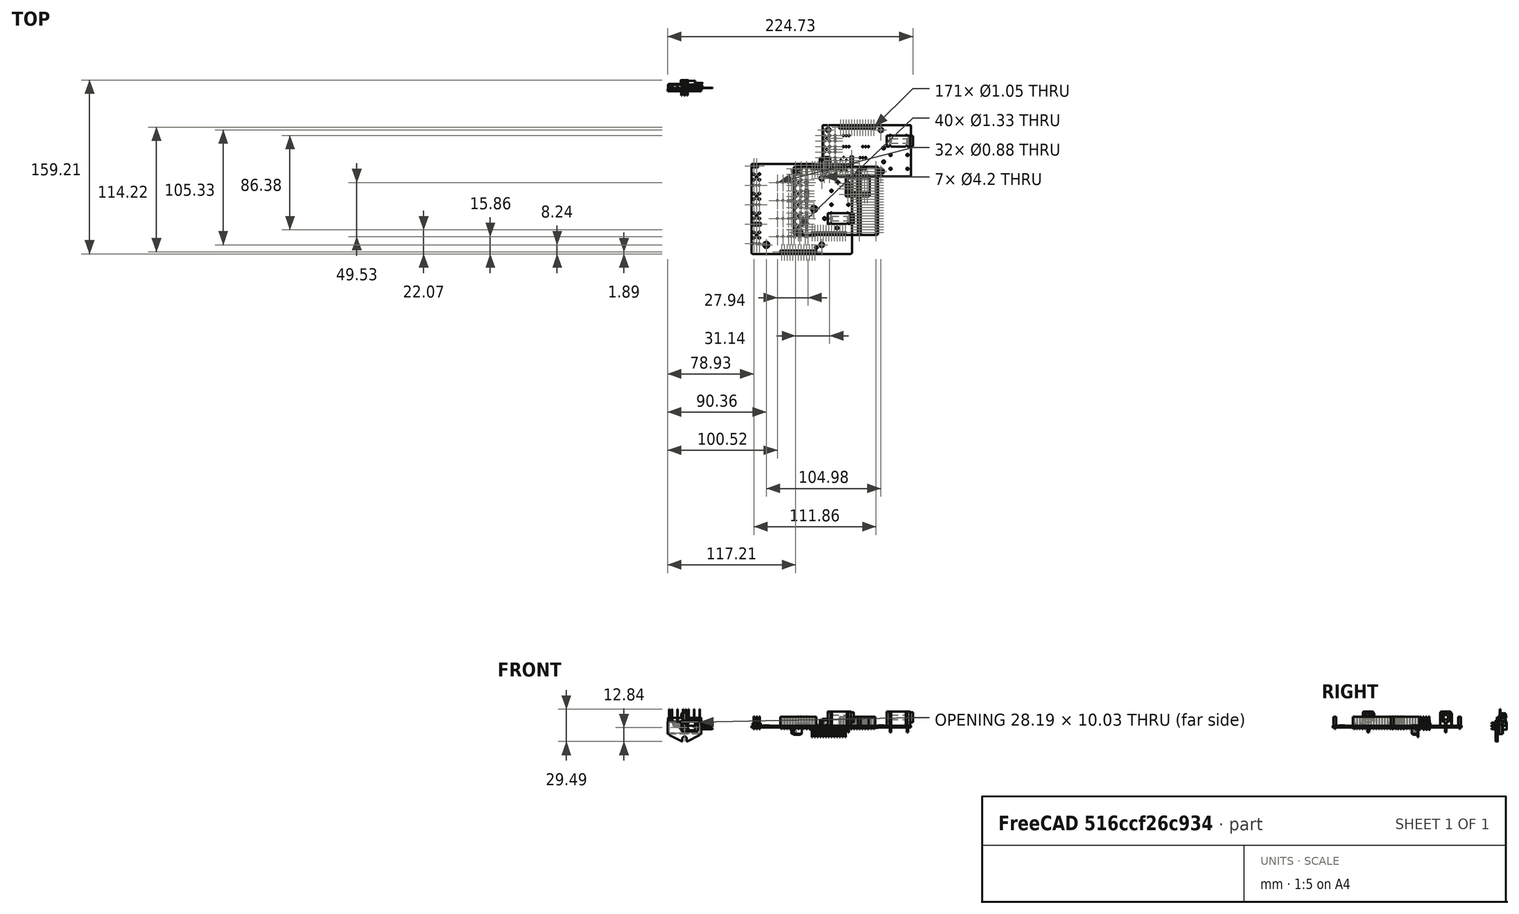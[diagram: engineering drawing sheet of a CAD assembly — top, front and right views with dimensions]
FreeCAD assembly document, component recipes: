
FREECAD ASSEMBLY — COMPONENT RECIPES ("KiCadStepUp")

This assembly document has 4 components, labeled P0..P3 below (a component is one placed body or linked part). 0 of them carry a construction recipe — the FreeCAD feature program that regenerates the part from scratch, quoted from this document or its linked companion documents; the rest are supplied as boundary geometry only. No exploded tour is included for this assembly.
COMPONENT P0 — geometry summary ("TIA1"; no construction recipe available for this part):
  bounding box: 21.8 x 19.0 x 11.6 mm
  tessellated surface: 5,376 triangles
  volume: 1532 mm^3 (32% of its bounding box)
  symmetry: mirror-symmetric across its x mid-plane
COMPONENT P1 — geometry summary ("HighVoltageBoard"; no construction recipe available for this part):
  bounding box: 100.7 x 82.5 x 29.5 mm
  tessellated surface: 122,468 triangles
  volume: 30977 mm^3 (13% of its bounding box)
COMPONENT P2 — geometry summary ("MainBoard"; no construction recipe available for this part):
  bounding box: 79.5 x 62.5 x 18.9 mm
  tessellated surface: 98,262 triangles
  volume: 13681 mm^3 (15% of its bounding box)
COMPONENT P3 — geometry summary ("PowerBoard"; no construction recipe available for this part):
  bounding box: 85.4 x 47.1 x 28.7 mm
  tessellated surface: 83,744 triangles
  volume: 18437 mm^3 (16% of its bounding box)
PROVENANCE & LICENSES
A FreeCAD (.FCStd) document from a public repository crawl; recipes are the document's own serialized feature recipes (and, for linked parts, companion documents' recipes).
License: mit.
